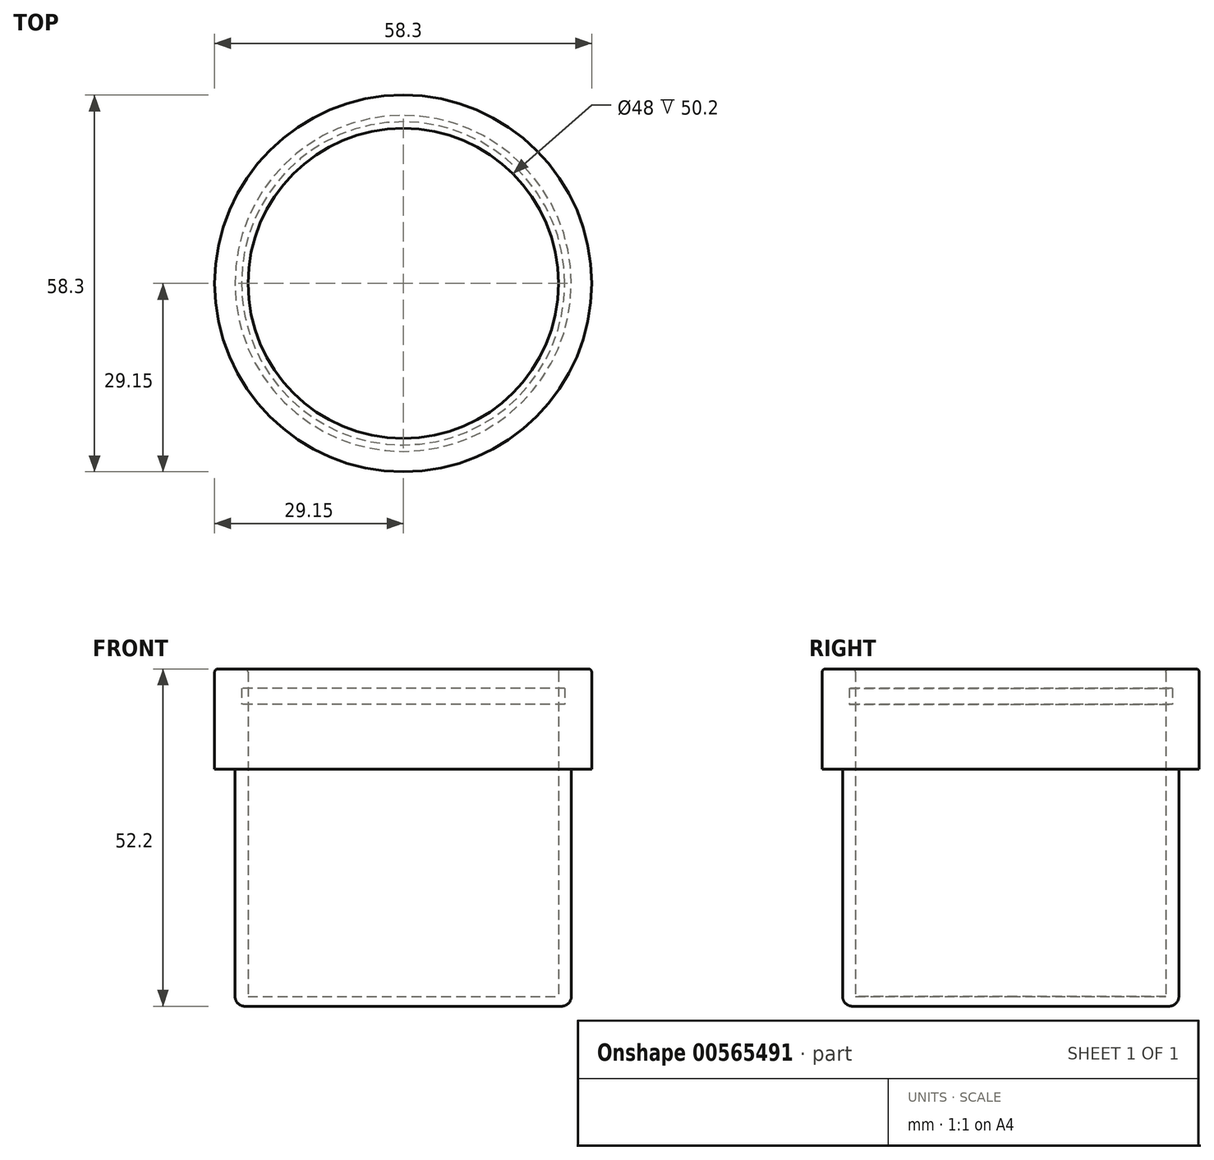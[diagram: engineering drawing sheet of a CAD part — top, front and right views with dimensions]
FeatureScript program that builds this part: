
annotation { "Feature Type Name" : "Feature", "Feature Type Description" : "" }
export const myFeature = defineFeature(function(context is Context, id is Id, definition is map)
    precondition{}
    {
        {
            var Q0;
            Q0=qCreatedBy(makeId("Top.planeOp"),FACE);
            var sketch = newSketch(context, id + "F0", { "sketchPlane" : qUnion([Q0])});
            skCircle(sketch, "E0", {"center": v(0, 0) * mm, "radius": 29.15 * mm});
            skCircle(sketch, "E1", {"center": v(0, 0) * mm, "radius": 24 * mm});
            skSolve(sketch);
        }
        {
            var Q0;
            Q0=makeQuery(id+"F0.imprint","IMPRINT",FACE,{"disambiguationData":[TD([[makeQuery(id+"F0.imprint","IMPRINT",EDGE,{"derivedFrom":sQuery(id+"F0.wireOp",EDGE,"E0")}),1.0]])]});
            extrude(context, id + "F1", {"entities" : qUnion([Q0]), "depth" : 15.5 * mm, "offsetDistance" : 25 * mm});
        }
        {
            var Q0;
            Q0=qCreatedBy(makeId("Top.planeOp"),FACE);
            cPlane(context, id + "F2", {"entities" : qUnion([Q0]), "cplaneType" : CPlaneType.OFFSET, "offset" : 10 * mm, "width" : 150 * mm, "height" : 150 * mm});
        }
        {
            var Q0;
            Q0=qCreatedBy(id+"F2.planeOp",FACE);
            var sketch = newSketch(context, id + "F3", { "sketchPlane" : qUnion([Q0])});
            skCircle(sketch, "E2", {"center": v(0, 0) * mm, "radius": 25 * mm});
            skSolve(sketch);
        }
        {
            var Q0;
            Q0=makeQuery(id+"F3.imprint","IMPRINT",FACE,{"disambiguationData":[TD([[makeQuery(id+"F3.imprint","IMPRINT",EDGE,{"derivedFrom":sQuery(id+"F3.wireOp",EDGE,"E2")}),1.0]])]});
            extrude(context, id + "F4", {"entities" : qUnion([Q0]), "depth" : 2.5 * mm, "offsetDistance" : 25 * mm});
        }
        {
            var Q0;
            Q0=makeQuery(id+"F1.opExtrude","CAP_FACE",FACE,{"disambiguationData":[OSD([sQuery(id+"F0.wireOp",EDGE,"E0"),sQuery(id+"F0.wireOp",EDGE,"E1")])],"isStart":true});
            var sketch = newSketch(context, id + "F5", { "sketchPlane" : qUnion([Q0])});
            skCircle(sketch, "E3", {"center": v(0, 0) * mm, "radius": 26 * mm});
            skCircle(sketch, "E4", {"center": v(0, 0) * mm, "radius": 24 * mm});
            skSolve(sketch);
        }
        {
            var Q0;
            Q0 = qSketchRegion(id + "F5", true);
            extrude(context, id + "F6", {"entities" : qUnion([Q0]), "operationType" : NewBodyOperationType.ADD, "depth" : (52.2 - 15.5) * mm, "offsetDistance" : 25 * mm});
        }
        {
            var Q0;
            Q0=makeQuery(id+"F6.opExtrude","CAP_FACE",FACE,{"disambiguationData":[OSD([sQuery(id+"F5.wireOp",EDGE,"E3"),sQuery(id+"F5.wireOp",EDGE,"E4")])],"isStart":false});
            var sketch = newSketch(context, id + "F7", { "sketchPlane" : qUnion([Q0])});
            skCircle(sketch, "E5", {"center": v(0, 0) * mm, "radius": 25.5 * mm});
            skSolve(sketch);
        }
        {
            var Q0;
            Q0 = qSketchRegion(id + "F7", true);
            extrude(context, id + "F8", {"entities" : qUnion([Q0]), "operationType" : NewBodyOperationType.ADD, "oppositeDirection" : true, "depth" : 1.5 * mm, "offsetDistance" : 25 * mm});
        }
        {
            var Q0;
            Q0=makeQuery(id+"F6.opExtrude","CAP_EDGE",EDGE,{"disambiguationData":[OSD([sQuery(id+"F5.wireOp",EDGE,"E3")])],"isStart":false});
            fillet(context, id + "F9", {"entities" : qUnion([Q0]), "radius" : 1.5 * mm, "tangentPropagation" : true, "allowEdgeOverflow" : false});
        }
        {
            var Q0;
            Q0=makeQuery(id+"F1.opExtrude","CAP_EDGE",EDGE,{"disambiguationData":[OSD([sQuery(id+"F0.wireOp",EDGE,"E0")])],"isStart":false});
            var Q1;
            Q1=makeQuery(id+"F1.opExtrude","CAP_EDGE",EDGE,{"disambiguationData":[OSD([sQuery(id+"F0.wireOp",EDGE,"E1")])],"isStart":false});
            fillet(context, id + "F10", {"entities" : qUnion([Q0, Q1]), "radius" : .5 * mm, "tangentPropagation" : true, "allowEdgeOverflow" : false});
        }
    });
